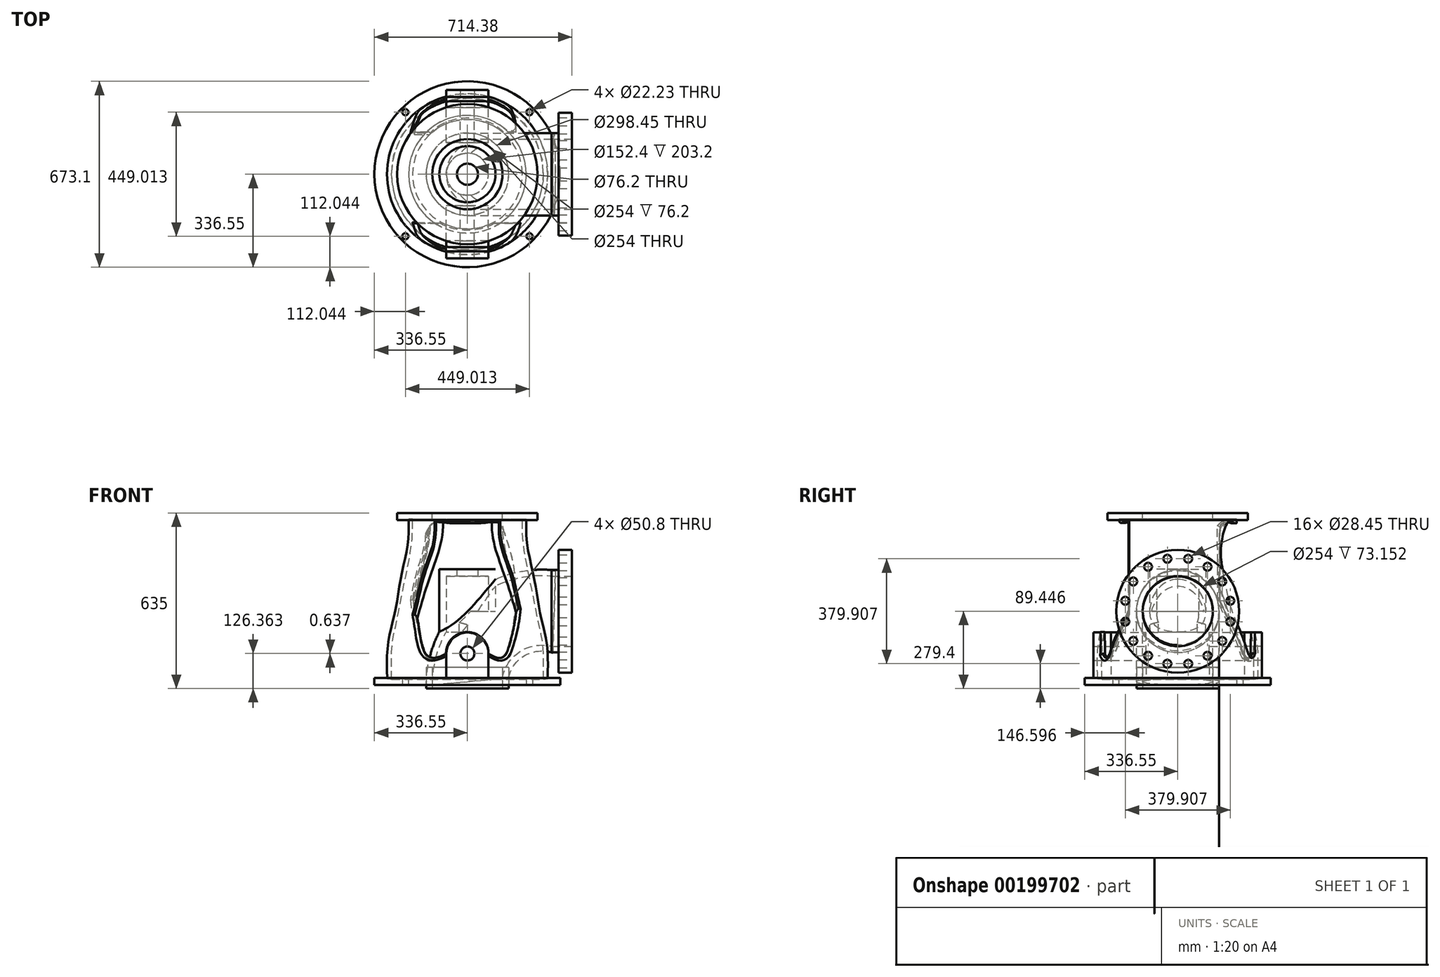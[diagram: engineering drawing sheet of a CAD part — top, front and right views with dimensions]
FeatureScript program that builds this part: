
annotation { "Feature Type Name" : "Feature", "Feature Type Description" : "" }
export const myFeature = defineFeature(function(context is Context, id is Id, definition is map)
    precondition{}
    {
        {
            var Q0;
            Q0=qCreatedBy(makeId("Top.planeOp"),FACE);
            var sketch = newSketch(context, id + "F0", { "sketchPlane" : qUnion([Q0])});
            skCircle(sketch, "E0", {"center": v(0, 0) * mm, "radius": 336.55 * mm});
            skCircle(sketch, "E1", {"center": v(0, 0) * mm, "radius": 149.23 * mm});
            skCircle(sketch, "E2", {"center": v(224.5, 224.5) * mm, "radius": 11.11 * mm});
            skCircle(sketch, "E3.1.0", {"center": v(-224.5, 224.5) * mm, "radius": 11.11 * mm});
            skCircle(sketch, "E3.2.0", {"center": v(-224.5, -224.5) * mm, "radius": 11.11 * mm});
            skCircle(sketch, "E3.3.0", {"center": v(224.5, -224.5) * mm, "radius": 11.11 * mm});
            skSolve(sketch);
        }
        {
            var Q0;
            Q0 = qSketchRegion(id + "F0", true);
            extrude(context, id + "F1", {"entities" : qUnion([Q0]), "depth" : 25.4 * mm});
        }
        {
            var Q0;
            Q0=qCreatedBy(makeId("Right.planeOp"),FACE);
            cPlane(context, id + "F2", {"entities" : qUnion([Q0]), "cplaneType" : CPlaneType.OFFSET, "offset" : 377.82 * mm, "width" : 152.4 * mm, "height" : 152.4 * mm});
        }
        {
            var Q0;
            Q0=qCreatedBy(id+"F2.planeOp",FACE);
            var sketch = newSketch(context, id + "F3", { "sketchPlane" : qUnion([Q0])});
            skCircle(sketch, "E4", {"center": v(0, 266.7) * mm, "radius": 127 * mm});
            skCircle(sketch, "E5", {"center": v(0, 266.7) * mm, "radius": 222.25 * mm});
            skCircle(sketch, "E6", {"center": v(37.78, 456.65) * mm, "radius": 14.22 * mm});
            skCircle(sketch, "E7.1.0", {"center": v(-37.78, 456.65) * mm, "radius": 14.22 * mm});
            skCircle(sketch, "E7.2.0", {"center": v(-107.6, 427.73) * mm, "radius": 14.22 * mm});
            skCircle(sketch, "E7.3.0", {"center": v(-161.03, 374.3) * mm, "radius": 14.22 * mm});
            skCircle(sketch, "E7.4.0", {"center": v(-189.95, 304.48) * mm, "radius": 14.22 * mm});
            skCircle(sketch, "E7.5.0", {"center": v(-189.95, 228.92) * mm, "radius": 14.22 * mm});
            skCircle(sketch, "E7.6.0", {"center": v(-161.03, 159.1) * mm, "radius": 14.22 * mm});
            skCircle(sketch, "E7.7.0", {"center": v(-107.6, 105.67) * mm, "radius": 14.22 * mm});
            skCircle(sketch, "E7.8.0", {"center": v(-37.78, 76.75) * mm, "radius": 14.22 * mm});
            skCircle(sketch, "E7.9.0", {"center": v(37.78, 76.75) * mm, "radius": 14.22 * mm});
            skCircle(sketch, "E7.10.0", {"center": v(107.6, 105.67) * mm, "radius": 14.22 * mm});
            skCircle(sketch, "E7.11.0", {"center": v(161.03, 159.1) * mm, "radius": 14.22 * mm});
            skCircle(sketch, "E7.12.0", {"center": v(189.95, 228.92) * mm, "radius": 14.22 * mm});
            skCircle(sketch, "E7.13.0", {"center": v(189.95, 304.48) * mm, "radius": 14.22 * mm});
            skCircle(sketch, "E7.14.0", {"center": v(161.03, 374.3) * mm, "radius": 14.22 * mm});
            skCircle(sketch, "E7.15.0", {"center": v(107.6, 427.73) * mm, "radius": 14.22 * mm});
            skSolve(sketch);
        }
        {
            var Q0;
            Q0 = qSketchRegion(id + "F3", true);
            extrude(context, id + "F4", {"entities" : qUnion([Q0]), "oppositeDirection" : true, "depth" : 47.75 * mm});
        }
        {
            var Q0;
            Q0=makeQuery(id+"F4.opExtrude","CAP_FACE",FACE,{"disambiguationData":[OSD([sQuery(id+"F3.wireOp",EDGE,"E4"),sQuery(id+"F3.wireOp",EDGE,"E5"),sQuery(id+"F3.wireOp",EDGE,"E6"),sQuery(id+"F3.wireOp",EDGE,"E7.1.0"),sQuery(id+"F3.wireOp",EDGE,"E7.2.0"),sQuery(id+"F3.wireOp",EDGE,"E7.3.0"),sQuery(id+"F3.wireOp",EDGE,"E7.4.0"),sQuery(id+"F3.wireOp",EDGE,"E7.5.0"),sQuery(id+"F3.wireOp",EDGE,"E7.6.0"),sQuery(id+"F3.wireOp",EDGE,"E7.7.0"),sQuery(id+"F3.wireOp",EDGE,"E7.8.0"),sQuery(id+"F3.wireOp",EDGE,"E7.9.0"),sQuery(id+"F3.wireOp",EDGE,"E7.10.0"),sQuery(id+"F3.wireOp",EDGE,"E7.11.0"),sQuery(id+"F3.wireOp",EDGE,"E7.12.0"),sQuery(id+"F3.wireOp",EDGE,"E7.13.0"),sQuery(id+"F3.wireOp",EDGE,"E7.14.0"),sQuery(id+"F3.wireOp",EDGE,"E7.15.0")])],"isStart":false});
            var sketch = newSketch(context, id + "F5", { "sketchPlane" : qUnion([Q0])});
            skCircle(sketch, "E8", {"center": v(0, 266.7) * mm, "radius": 127 * mm});
            skCircle(sketch, "E9", {"center": v(0, 266.7) * mm, "radius": 149.23 * mm});
            skSolve(sketch);
        }
        {
            var Q0;
            Q0 = qSketchRegion(id + "F5", true);
            extrude(context, id + "F6", {"entities" : qUnion([Q0]), "operationType" : NewBodyOperationType.ADD, "depth" : 25.4 * mm});
        }
        {
            var Q0;
            Q0=makeQuery(id+"F1.opExtrude","CAP_FACE",FACE,{"disambiguationData":[OSD([sQuery(id+"F0.wireOp",EDGE,"E0"),sQuery(id+"F0.wireOp",EDGE,"E1"),sQuery(id+"F0.wireOp",EDGE,"E2"),sQuery(id+"F0.wireOp",EDGE,"E3.1.0"),sQuery(id+"F0.wireOp",EDGE,"E3.2.0"),sQuery(id+"F0.wireOp",EDGE,"E3.3.0")])],"isStart":false});
            var sketch = newSketch(context, id + "F7", { "sketchPlane" : qUnion([Q0])});
            skCircle(sketch, "E10", {"center": v(0, 0) * mm, "radius": 149.23 * mm});
            skCircle(sketch, "E11", {"center": v(0, 0) * mm, "radius": 127 * mm});
            skSolve(sketch);
        }
        {
            var Q0;
            Q0 = qSketchRegion(id + "F7", true);
            extrude(context, id + "F8", {"entities" : qUnion([Q0]), "endBound" : BoundingType.SYMMETRIC, "depth" : 76.2 * mm});
        }
        {
            var Q0;
            Q0=makeQuery(id+"F8.opExtrude","CAP_FACE",FACE,{"disambiguationData":[OSD([sQuery(id+"F7.wireOp",EDGE,"E10"),sQuery(id+"F7.wireOp",EDGE,"E11")])],"isStart":false});
            cPlane(context, id + "F9", {"entities" : qUnion([Q0]), "cplaneType" : CPlaneType.OFFSET, "offset" : 0 * mm, "width" : 152.4 * mm, "height" : 152.4 * mm});
        }
        {
            var Q0;
            Q0=qCreatedBy(makeId("Front.planeOp"),FACE);
            var sketch = newSketch(context, id + "F10", { "sketchPlane" : qUnion([Q0])});
            skPoint(sketch, "E12.second.point", {"position": v(385.69, 128.56) * mm});
            skPoint(sketch, "E12.third.point", {"position": v(188.91, 266.7) * mm});
            skArc(sketch, "E13", {"start": v(302.1, 266.7) * mm, "mid": v(90.9, 201.49) * mm, "end": v(0, 0) * mm});
            skSolve(sketch);
        }
        {
            var Q0;
            Q0=makeQuery(id+"F6.opExtrude","CAP_FACE",FACE,{"disambiguationData":[OSD([sQuery(id+"F5.wireOp",EDGE,"E8"),sQuery(id+"F5.wireOp",EDGE,"E9")])],"isStart":false});
            var Q1;
            Q1=sQuery(id+"F10.wireOp",EDGE,"E13");
            sweep(context, id + "F11", {"profiles" : qUnion([Q0]), "path" : qUnion([Q1])});
        }
        {
            var Q0;
            Q0=qCreatedBy(id+"F9.planeOp",FACE);
            cPlane(context, id + "F12", {"entities" : qUnion([Q0]), "cplaneType" : CPlaneType.OFFSET, "offset" : 203.2 * mm, "width" : 152.4 * mm, "height" : 152.4 * mm});
        }
        {
            var Q0;
            Q0=qCreatedBy(id+"F12.planeOp",FACE);
            var sketch = newSketch(context, id + "F13", { "sketchPlane" : qUnion([Q0])});
            skCircle(sketch, "E14", {"center": v(0, 0) * mm, "radius": 101.6 * mm});
            skCircle(sketch, "E15", {"center": v(0, 0) * mm, "radius": 76.2 * mm});
            skSolve(sketch);
        }
        {
            var Q0;
            Q0 = qSketchRegion(id + "F13", true);
            extrude(context, id + "F14", {"entities" : qUnion([Q0]), "operationType" : NewBodyOperationType.ADD, "depth" : 127 * mm});
        }
        {
            var Q0;
            {var subQ0=sQuery(id+"F13.wireOp",EDGE,"E14");var subQ1=sQuery(id+"F13.wireOp",EDGE,"E15");Q0=makeQuery(id+"F14.boolean.opBoolean","SPLIT",FACE,{"disambiguationData":[TD([makeQuery(id+"F11.opSweep","SWEPT_FACE",FACE,{"disambiguationData":[OSD([sQuery(id+"F5.wireOp",EDGE,"E9"),sQuery(id+"F10.wireOp",EDGE,"E13")])]})])],"derivedFrom":makeQuery(id+"F14.opExtrude","CAP_FACE",FACE,{"disambiguationData":[OSD([subQ0,subQ1])],"isStart":true})});}
            extrude(context, id + "F15", {"entities" : qUnion([Q0]), "operationType" : NewBodyOperationType.ADD, "depth" : 76.2 * mm});
        }
        {
            var Q0;
            Q0=makeQuery(id+"F14.opExtrude","CAP_FACE",FACE,{"disambiguationData":[OSD([sQuery(id+"F13.wireOp",EDGE,"E14"),sQuery(id+"F13.wireOp",EDGE,"E15")])],"isStart":false});
            var sketch = newSketch(context, id + "F16", { "sketchPlane" : qUnion([Q0])});
            skCircle(sketch, "E16", {"center": v(0, 0) * mm, "radius": 76.2 * mm});
            skSolve(sketch);
        }
        {
            var Q0;
            Q0 = qSketchRegion(id + "F16", true);
            extrude(context, id + "F17", {"entities" : qUnion([Q0]), "operationType" : NewBodyOperationType.REMOVE, "oppositeDirection" : true, "depth" : 355.6 * mm});
        }
        {
            var Q0;
            Q0=makeQuery(id+"F14.opExtrude","CAP_FACE",FACE,{"disambiguationData":[OSD([sQuery(id+"F13.wireOp",EDGE,"E14"),sQuery(id+"F13.wireOp",EDGE,"E15")])],"isStart":false});
            var sketch = newSketch(context, id + "F18", { "sketchPlane" : qUnion([Q0])});
            skCircle(sketch, "E17", {"center": v(0, 0) * mm, "radius": 101.6 * mm});
            skCircle(sketch, "E18", {"center": v(0, 0) * mm, "radius": 38.1 * mm});
            skSolve(sketch);
        }
        {
            var Q0;
            Q0 = qSketchRegion(id + "F18", true);
            extrude(context, id + "F19", {"entities" : qUnion([Q0]), "operationType" : NewBodyOperationType.ADD, "depth" : 25.4 * mm});
        }
        {
            var Q0;
            Q0=makeQuery(id+"F1.opExtrude","CAP_FACE",FACE,{"disambiguationData":[OSD([sQuery(id+"F0.wireOp",EDGE,"E0"),sQuery(id+"F0.wireOp",EDGE,"E1"),sQuery(id+"F0.wireOp",EDGE,"E2"),sQuery(id+"F0.wireOp",EDGE,"E3.1.0"),sQuery(id+"F0.wireOp",EDGE,"E3.2.0"),sQuery(id+"F0.wireOp",EDGE,"E3.3.0")])],"isStart":true});
            cPlane(context, id + "F20", {"entities" : qUnion([Q0]), "cplaneType" : CPlaneType.OFFSET, "offset" : 622.3 * mm, "oppositeDirection" : true, "width" : 152.4 * mm, "height" : 152.4 * mm});
        }
        {
            var Q0;
            Q0=qCreatedBy(id+"F20.planeOp",FACE);
            var sketch = newSketch(context, id + "F21", { "sketchPlane" : qUnion([Q0])});
            skCircle(sketch, "E19", {"center": v(0, 0) * mm, "radius": 254 * mm});
            skCircle(sketch, "E20", {"center": v(0, 0) * mm, "radius": 127 * mm});
            skSolve(sketch);
        }
        {
            var Q0;
            Q0 = qSketchRegion(id + "F21", true);
            extrude(context, id + "F22", {"entities" : qUnion([Q0]), "depth" : 25.4 * mm});
        }
        {
            var Q0;
            Q0=qCreatedBy(makeId("Front.planeOp"),FACE);
            var sketch = newSketch(context, id + "F23", { "sketchPlane" : qUnion([Q0])});
            skLineSegment(sketch, "E21", {"start": v(0, -107.58) * mm, "end": v(0, 784.96) * mm});
            skFitSpline(sketch, "E22", {"points": [v(-289.86, 22.9) * mm, v(-287.14, 150.67) * mm, v(-262.67, 261.21) * mm, v(-240.93, 388.07) * mm, v(-216.46, 505.87) * mm, v(-212.84, 601.01) * mm], "startDerivative": vector(-19.9, 627.3) * mm, "endDerivative": vector(-7.36, 515.78) * mm});
            skFitSpline(sketch, "E23", {"points": [v(-274.45, 20.18) * mm, v(-275.36, 84.52) * mm, v(-270.83, 161.54) * mm, v(-264.96, 189.94) * mm, v(-256.33, 229.5) * mm, v(-232.77, 348.2) * mm, v(-211.02, 454.22) * mm, v(-200.15, 533.96) * mm, v(-198.34, 600.1) * mm], "startDerivative": vector(-11.02, 493.44) * mm, "endDerivative": vector(1.24, 534.67) * mm});
            skLineSegment(sketch, "E24", {"start": v(-274.45, 20.18) * mm, "end": v(-289.86, 22.9) * mm});
            skLineSegment(sketch, "E25", {"start": v(-198.34, 600.1) * mm, "end": v(-212.84, 601.01) * mm});
            skSolve(sketch);
        }
        {
            var Q0;
            Q0 = qSketchRegion(id + "F23", true);
            var Q1;
            Q1=sQuery(id+"F23.wireOp",EDGE,"E21");
            revolve(context, id + "F24", {"entities" : qUnion([Q0]), "axis" : qUnion([Q1]), "revolveType" : RevolveType.FULL});
        }
        {
            var Q0;
            Q0=qCreatedBy(makeId("Front.planeOp"),FACE);
            cPlane(context, id + "F25", {"entities" : qUnion([Q0]), "cplaneType" : CPlaneType.OFFSET, "offset" : 177.8 * mm, "width" : 152.4 * mm, "height" : 152.4 * mm});
        }
        {
            var Q0;
            Q0=qCreatedBy(makeId("Front.planeOp"),FACE);
            cPlane(context, id + "F26", {"entities" : qUnion([Q0]), "cplaneType" : CPlaneType.OFFSET, "offset" : 177.8 * mm, "oppositeDirection" : true, "width" : 152.4 * mm, "height" : 152.4 * mm});
        }
        {
            var Q0;
            Q0=qCreatedBy(id+"F25.planeOp",FACE);
            var sketch = newSketch(context, id + "F27", { "sketchPlane" : qUnion([Q0])});
            skLineSegment(sketch, "E26", {"start": v(0, 24.76) * mm, "end": v(-76.2, 24.76) * mm});
            skLineSegment(sketch, "E27", {"start": v(-76.2, 24.76) * mm, "end": v(-76.2, 113.66) * mm});
            skLineSegment(sketch, "E28", {"start": v(76.2, 113.66) * mm, "end": v(76.2, 24.76) * mm});
            skLineSegment(sketch, "E29", {"start": v(76.2, 24.76) * mm, "end": v(-76.2, 24.76) * mm});
            skArc(sketch, "E30", {"start": v(76.2, 113.66) * mm, "mid": v(0, 189.86) * mm, "end": v(-76.2, 113.66) * mm});
            skCircle(sketch, "E31", {"center": v(0, 113.66) * mm, "radius": 25.4 * mm});
            skSolve(sketch);
        }
        {
            var Q0;
            Q0 = qSketchRegion(id + "F27", true);
            extrude(context, id + "F28", {"entities" : qUnion([Q0]), "endBound" : BoundingType.SYMMETRIC, "depth" : 127 * mm});
        }
        {
            var Q0;
            Q0=makeQuery(id+"F28.opExtrude","CAP_FACE",FACE,{"disambiguationData":[OSD([sQuery(id+"F27.wireOp",EDGE,"E27"),sQuery(id+"F27.wireOp",EDGE,"E28"),sQuery(id+"F27.wireOp",EDGE,"E29"),sQuery(id+"F27.wireOp",EDGE,"E30"),sQuery(id+"F27.wireOp",EDGE,"E31")])],"isStart":false});
            extrude(context, id + "F29", {"entities" : qUnion([Q0]), "depth" : 63.5 * mm});
        }
        {
            var Q0;
            Q0=qCreatedBy(id+"F26.planeOp",FACE);
            var sketch = newSketch(context, id + "F30", { "sketchPlane" : qUnion([Q0])});
            skLineSegment(sketch, "E32", {"start": v(0, 25.4) * mm, "end": v(76.2, 25.4) * mm});
            skLineSegment(sketch, "E33", {"start": v(76.2, 25.4) * mm, "end": v(76.2, 114.3) * mm});
            skLineSegment(sketch, "E34", {"start": v(-76.2, 114.3) * mm, "end": v(-76.2, 25.4) * mm});
            skLineSegment(sketch, "E35", {"start": v(-76.2, 25.4) * mm, "end": v(0, 25.4) * mm});
            skArc(sketch, "E36", {"start": v(76.2, 114.3) * mm, "mid": v(0, 190.5) * mm, "end": v(-76.2, 114.3) * mm});
            skCircle(sketch, "E37", {"center": v(0, 114.3) * mm, "radius": 25.4 * mm});
            skSolve(sketch);
        }
        {
            var Q0;
            Q0 = qSketchRegion(id + "F30", true);
            extrude(context, id + "F31", {"entities" : qUnion([Q0]), "endBound" : BoundingType.SYMMETRIC, "depth" : 127 * mm});
        }
        {
            var Q0;
            Q0=makeQuery(id+"F31.opExtrude","CAP_FACE",FACE,{"disambiguationData":[OSD([sQuery(id+"F30.wireOp",EDGE,"E32"),sQuery(id+"F30.wireOp",EDGE,"E33"),sQuery(id+"F30.wireOp",EDGE,"E34"),sQuery(id+"F30.wireOp",EDGE,"E35"),sQuery(id+"F30.wireOp",EDGE,"E36"),sQuery(id+"F30.wireOp",EDGE,"E37")])],"isStart":true});
            extrude(context, id + "F32", {"entities" : qUnion([Q0]), "depth" : 63.5 * mm});
        }
        {
            var Q0;
            Q0=makeQuery(id+"F32.opExtrude","CAP_FACE",FACE,{"disambiguationData":[OSD([sQuery(id+"F30.wireOp",EDGE,"E32"),sQuery(id+"F30.wireOp",EDGE,"E33"),sQuery(id+"F30.wireOp",EDGE,"E34"),sQuery(id+"F30.wireOp",EDGE,"E35"),sQuery(id+"F30.wireOp",EDGE,"E36"),sQuery(id+"F30.wireOp",EDGE,"E37")])],"isStart":false});
            var sketch = newSketch(context, id + "F33", { "sketchPlane" : qUnion([Q0])});
            skArc(sketch, "E38", {"start": v(76.2, 114.3) * mm, "mid": v(0, 190.5) * mm, "end": v(-76.2, 114.3) * mm});
            skFitSpline(sketch, "E39", {"points": [v(-76.2, 114.3) * mm, v(-104.03, 99.37) * mm, v(-135.63, 108.14) * mm, v(-174.25, 365.3) * mm, v(-146.16, 514.52) * mm, v(-111.05, 587.37) * mm, v(-66.3, 587.37) * mm, v(0, 585.61) * mm, v(59.22, 585.61) * mm, v(123.3, 583.85) * mm, v(160.15, 525.93) * mm, v(190, 409.2) * mm, v(187.36, 286.32) * mm, v(172.44, 188.01) * mm, v(139.97, 97.61) * mm, v(107.5, 100.24) * mm, v(76.2, 114.3) * mm], "startDerivative": vector(-673.7, -447.67) * mm, "endDerivative": vector(-677.97, 562.8) * mm});
            skSolve(sketch);
        }
        {
            var Q0;
            Q0 = qSketchRegion(id + "F33", true);
            extrude(context, id + "F34", {"entities" : qUnion([Q0]), "operationType" : NewBodyOperationType.REMOVE, "oppositeDirection" : true, "depth" : 152.4 * mm});
        }
        {
            var Q0;
            Q0=qCreatedBy(id+"F25.planeOp",FACE);
            var sketch = newSketch(context, id + "F35", { "sketchPlane" : qUnion([Q0])});
            skArc(sketch, "E40", {"start": v(76.24, 112.57) * mm, "mid": v(-0.63, 191.43) * mm, "end": v(-77.5, 112.57) * mm});
            skFitSpline(sketch, "E41", {"points": [v(-77.5, 112.57) * mm, v(-117.37, 98.33) * mm, v(-151.53, 112.57) * mm, v(-176.2, 214.12) * mm, v(-188.54, 297.63) * mm, v(-184.75, 393.49) * mm, v(-150.58, 529.2) * mm, v(-139.2, 574.76) * mm, v(-105.98, 589) * mm, v(-61.37, 587.1) * mm, v(-45.24, 586.15) * mm, v(21.2, 587.1) * mm, v(97.12, 589) * mm, v(126.54, 576.66) * mm, v(142.68, 526.36) * mm, v(169.25, 433.35) * mm, v(176.84, 340.34) * mm, v(172.1, 235.95) * mm, v(146.47, 128.7) * mm, v(133.18, 104.03) * mm, v(116.1, 97.38) * mm, v(98.07, 102.13) * mm, v(76.24, 112.57) * mm], "startDerivative": vector(-1012.73, -495.32) * mm, "endDerivative": vector(-751.27, 373.43) * mm});
            skSolve(sketch);
        }
        {
            var Q0;
            Q0 = qSketchRegion(id + "F35", true);
            extrude(context, id + "F36", {"entities" : qUnion([Q0]), "operationType" : NewBodyOperationType.REMOVE, "depth" : 203.2 * mm});
        }
        {
            var Q0;
            Q0=makeQuery(id+"F36.boolean.opBoolean","INTERSECT",EDGE,{"disambiguationData":[OD(1.0)],"derivedFrom":[makeQuery(id+"F24.opRevolve","SWEPT_FACE",FACE,{"disambiguationData":[OSD([sQuery(id+"F23.wireOp",EDGE,"E22")])]}),makeQuery(id+"F36.opExtrude","SWEPT_FACE",FACE,{"disambiguationData":[OSD([sQuery(id+"F35.wireOp",EDGE,"E41")])]})]});
            var Q1;
            Q1=makeQuery(id+"F36.boolean.opBoolean","INTERSECT",EDGE,{"disambiguationData":[OD(1.0)],"derivedFrom":[makeQuery(id+"F24.opRevolve","SWEPT_FACE",FACE,{"disambiguationData":[OSD([sQuery(id+"F23.wireOp",EDGE,"E22")])]}),makeQuery(id+"F36.opExtrude","CAP_FACE",FACE,{"disambiguationData":[OSD([sQuery(id+"F35.wireOp",EDGE,"E40"),sQuery(id+"F35.wireOp",EDGE,"E41")])],"isStart":true})]});
            var Q2;
            Q2=makeQuery(id+"F36.boolean.opBoolean","INTERSECT",EDGE,{"disambiguationData":[OD(0.0)],"derivedFrom":[makeQuery(id+"F24.opRevolve","SWEPT_FACE",FACE,{"disambiguationData":[OSD([sQuery(id+"F23.wireOp",EDGE,"E22")])]}),makeQuery(id+"F36.opExtrude","SWEPT_FACE",FACE,{"disambiguationData":[OSD([sQuery(id+"F35.wireOp",EDGE,"E41")])]})]});
            var Q3;
            Q3=makeQuery(id+"F36.boolean.opBoolean","INTERSECT",EDGE,{"disambiguationData":[OD(0.0)],"derivedFrom":[makeQuery(id+"F24.opRevolve","SWEPT_FACE",FACE,{"disambiguationData":[OSD([sQuery(id+"F23.wireOp",EDGE,"E22")])]}),makeQuery(id+"F36.opExtrude","CAP_FACE",FACE,{"disambiguationData":[OSD([sQuery(id+"F35.wireOp",EDGE,"E40"),sQuery(id+"F35.wireOp",EDGE,"E41")])],"isStart":true})]});
            var Q4;
            Q4=makeQuery(id+"F36.boolean.opBoolean","INTERSECT",EDGE,{"disambiguationData":[OD(2.0)],"derivedFrom":[makeQuery(id+"F24.opRevolve","SWEPT_FACE",FACE,{"disambiguationData":[OSD([sQuery(id+"F23.wireOp",EDGE,"E22")])]}),makeQuery(id+"F36.opExtrude","SWEPT_FACE",FACE,{"disambiguationData":[OSD([sQuery(id+"F35.wireOp",EDGE,"E41")])]})]});
            var Q5;
            Q5=makeQuery(id+"F34.boolean.opBoolean","INTERSECT",EDGE,{"disambiguationData":[OD(1.0)],"derivedFrom":[makeQuery(id+"F24.opRevolve","SWEPT_FACE",FACE,{"disambiguationData":[OSD([sQuery(id+"F23.wireOp",EDGE,"E22")])]}),makeQuery(id+"F34.opExtrude","SWEPT_FACE",FACE,{"disambiguationData":[OSD([sQuery(id+"F33.wireOp",EDGE,"E39")])]})]});
            var Q6;
            Q6=makeQuery(id+"F34.boolean.opBoolean","INTERSECT",EDGE,{"derivedFrom":[makeQuery(id+"F24.opRevolve","SWEPT_FACE",FACE,{"disambiguationData":[OSD([sQuery(id+"F23.wireOp",EDGE,"E22")])]}),makeQuery(id+"F34.opExtrude","CAP_FACE",FACE,{"disambiguationData":[OSD([sQuery(id+"F33.wireOp",EDGE,"E38"),sQuery(id+"F33.wireOp",EDGE,"E39")])],"isStart":false})]});
            fillet(context, id + "F37", {"entities" : qUnion([Q0, Q1, Q2, Q3, Q4, Q5, Q6]), "radius" : 9.52 * mm, "tangentPropagation" : true, "allowEdgeOverflow" : false});
        }
        {
            var Q0;
            Q0=makeQuery(id+"F34.boolean.opBoolean","INTERSECT",EDGE,{"disambiguationData":[OD(1.0)],"derivedFrom":[makeQuery(id+"F24.opRevolve","SWEPT_FACE",FACE,{"disambiguationData":[OSD([sQuery(id+"F23.wireOp",EDGE,"E23")])]}),makeQuery(id+"F34.opExtrude","CAP_FACE",FACE,{"disambiguationData":[OSD([sQuery(id+"F33.wireOp",EDGE,"E38"),sQuery(id+"F33.wireOp",EDGE,"E39")])],"isStart":false})]});
            fillet(context, id + "F38", {"entities" : qUnion([Q0]), "radius" : 5.08 * mm, "tangentPropagation" : true, "allowEdgeOverflow" : false});
        }
        {
            var Q0;
            Q0=makeQuery(id+"F34.boolean.opBoolean","INTERSECT",EDGE,{"disambiguationData":[OD(0.0)],"derivedFrom":[makeQuery(id+"F24.opRevolve","SWEPT_FACE",FACE,{"disambiguationData":[OSD([sQuery(id+"F23.wireOp",EDGE,"E23")])]}),makeQuery(id+"F34.opExtrude","SWEPT_FACE",FACE,{"disambiguationData":[OSD([sQuery(id+"F33.wireOp",EDGE,"E39")])]})]});
            fillet(context, id + "F39", {"entities" : qUnion([Q0]), "radius" : 5.08 * mm, "tangentPropagation" : true, "allowEdgeOverflow" : false});
        }
    });
